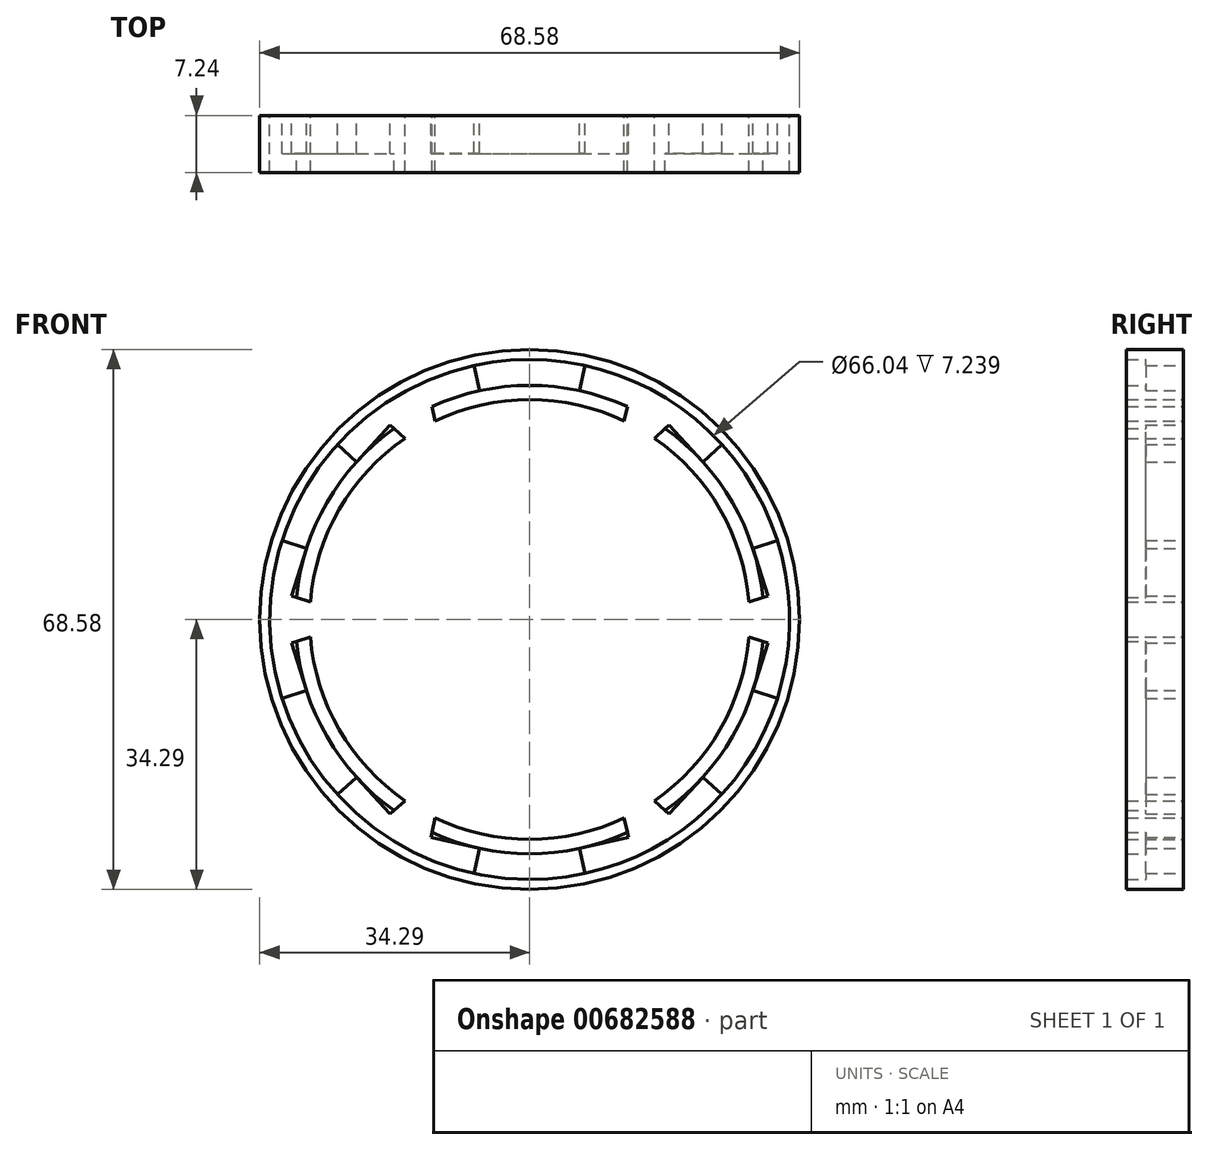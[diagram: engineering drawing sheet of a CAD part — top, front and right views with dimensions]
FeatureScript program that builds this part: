
annotation { "Feature Type Name" : "Feature", "Feature Type Description" : "" }
export const myFeature = defineFeature(function(context is Context, id is Id, definition is map)
    precondition{}
    {
        {
            var Q0;
            Q0=qCreatedBy(makeId("Front.planeOp"),FACE);
            var sketch = newSketch(context, id + "F0", { "sketchPlane" : qUnion([Q0])});
            skCircle(sketch, "E0", {"center": v(0, 0) * mm, "radius": 34.3 * mm});
            skArc(sketch, "E1", {"start": v(-15.84, 23.02) * mm, "mid": v(-24.2, 13.97) * mm, "end": v(-27.85, 2.21) * mm});
            skLineSegment(sketch, "E2", {"start": v(-7.05, 32.26) * mm, "end": v(-6.35, 29.06) * mm});
            skLineSegment(sketch, "E3", {"start": v(-6.35, 29.06) * mm, "end": v(-12.55, 27.7) * mm});
            skLineSegment(sketch, "E4", {"start": v(-12.55, 27.7) * mm, "end": v(-12.01, 25.23) * mm});
            skLineSegment(sketch, "E5", {"start": v(-18.86, 30.98) * mm, "end": v(0, 35.1) * mm, "construction": true});
            skLineSegment(sketch, "E6.MirrorCS", {"start": v(7.05, 32.26) * mm, "end": v(6.35, 29.06) * mm});
            skLineSegment(sketch, "E7.MirrorCS", {"start": v(6.35, 29.06) * mm, "end": v(12.55, 27.7) * mm});
            skLineSegment(sketch, "E8.MirrorCS", {"start": v(12.55, 27.7) * mm, "end": v(12.01, 25.23) * mm});
            skLineSegment(sketch, "E9.1.0", {"start": v(-31.46, 10.03) * mm, "end": v(-28.34, 9.03) * mm});
            skLineSegment(sketch, "E9.1.1", {"start": v(-28.34, 9.03) * mm, "end": v(-30.27, 2.98) * mm});
            skLineSegment(sketch, "E9.1.2", {"start": v(-30.27, 2.98) * mm, "end": v(-27.85, 2.21) * mm});
            skLineSegment(sketch, "E9.1.3", {"start": v(-17.72, 24.73) * mm, "end": v(-15.84, 23.02) * mm});
            skLineSegment(sketch, "E9.1.4", {"start": v(-22, 20.03) * mm, "end": v(-17.72, 24.73) * mm});
            skLineSegment(sketch, "E9.1.5", {"start": v(-24.41, 22.23) * mm, "end": v(-22, 20.03) * mm});
            skLineSegment(sketch, "E9.2.0", {"start": v(-24.41, -22.23) * mm, "end": v(-22, -20.03) * mm});
            skLineSegment(sketch, "E9.2.1", {"start": v(-22, -20.03) * mm, "end": v(-17.72, -24.73) * mm});
            skLineSegment(sketch, "E9.2.2", {"start": v(-17.72, -24.73) * mm, "end": v(-15.84, -23.02) * mm});
            skLineSegment(sketch, "E9.2.3", {"start": v(-30.27, -2.98) * mm, "end": v(-27.85, -2.21) * mm});
            skLineSegment(sketch, "E9.2.4", {"start": v(-28.34, -9.03) * mm, "end": v(-30.27, -2.98) * mm});
            skLineSegment(sketch, "E9.2.5", {"start": v(-31.46, -10.03) * mm, "end": v(-28.34, -9.03) * mm});
            skLineSegment(sketch, "E9.3.0", {"start": v(7.05, -32.26) * mm, "end": v(6.35, -29.06) * mm});
            skLineSegment(sketch, "E9.3.1", {"start": v(6.35, -29.06) * mm, "end": v(12.55, -27.7) * mm});
            skLineSegment(sketch, "E9.3.2", {"start": v(12.55, -27.7) * mm, "end": v(12.01, -25.23) * mm});
            skLineSegment(sketch, "E9.3.3", {"start": v(-12.55, -27.7) * mm, "end": v(-12.01, -25.23) * mm});
            skLineSegment(sketch, "E9.3.4", {"start": v(-6.35, -29.06) * mm, "end": v(-12.55, -27.7) * mm});
            skLineSegment(sketch, "E9.3.5", {"start": v(-7.05, -32.26) * mm, "end": v(-6.35, -29.06) * mm});
            skLineSegment(sketch, "E9.4.0", {"start": v(31.46, -10.03) * mm, "end": v(28.34, -9.03) * mm});
            skLineSegment(sketch, "E9.4.1", {"start": v(28.34, -9.03) * mm, "end": v(30.27, -2.98) * mm});
            skLineSegment(sketch, "E9.4.2", {"start": v(30.27, -2.98) * mm, "end": v(27.85, -2.21) * mm});
            skLineSegment(sketch, "E9.4.3", {"start": v(17.72, -24.73) * mm, "end": v(15.84, -23.02) * mm});
            skLineSegment(sketch, "E9.4.4", {"start": v(22, -20.03) * mm, "end": v(17.72, -24.73) * mm});
            skLineSegment(sketch, "E9.4.5", {"start": v(24.41, -22.23) * mm, "end": v(22, -20.03) * mm});
            skLineSegment(sketch, "E9.5.0", {"start": v(24.41, 22.23) * mm, "end": v(22, 20.03) * mm});
            skLineSegment(sketch, "E9.5.1", {"start": v(22, 20.03) * mm, "end": v(17.72, 24.73) * mm});
            skLineSegment(sketch, "E9.5.2", {"start": v(17.72, 24.73) * mm, "end": v(15.84, 23.02) * mm});
            skLineSegment(sketch, "E9.5.3", {"start": v(30.27, 2.98) * mm, "end": v(27.85, 2.21) * mm});
            skLineSegment(sketch, "E9.5.4", {"start": v(28.34, 9.03) * mm, "end": v(30.27, 2.98) * mm});
            skLineSegment(sketch, "E9.5.5", {"start": v(31.46, 10.03) * mm, "end": v(28.34, 9.03) * mm});
            skArc(sketch, "E10.trimOffspring", {"start": v(-27.85, -2.21) * mm, "mid": v(-24.2, -13.97) * mm, "end": v(-15.84, -23.02) * mm});
            skArc(sketch, "E11.trimOffspring", {"start": v(-12.01, -25.23) * mm, "mid": v(0, -27.94) * mm, "end": v(12.01, -25.23) * mm});
            skArc(sketch, "E12.trimOffspring", {"start": v(15.84, -23.02) * mm, "mid": v(24.2, -13.97) * mm, "end": v(27.85, -2.21) * mm});
            skArc(sketch, "E13.trimOffspring", {"start": v(27.85, 2.21) * mm, "mid": v(24.2, 13.97) * mm, "end": v(15.84, 23.02) * mm});
            skArc(sketch, "E14.trimOffspring", {"start": v(12.01, 25.23) * mm, "mid": v(0, 27.94) * mm, "end": v(-12.01, 25.23) * mm});
            skArc(sketch, "E15", {"start": v(-7.05, 32.26) * mm, "mid": v(-16.51, 28.6) * mm, "end": v(-24.41, 22.23) * mm});
            skPoint(sketch, "E16.orphan", {"position": v(7.32, 33.5) * mm});
            skPoint(sketch, "E17.orphan", {"position": v(-7.32, 33.5) * mm});
            skPoint(sketch, "E18.orphan", {"position": v(-25.35, 23.09) * mm});
            skArc(sketch, "E19.trimOffspring", {"start": v(-31.46, 10.03) * mm, "mid": v(-33.02, 0) * mm, "end": v(-31.46, -10.03) * mm});
            skPoint(sketch, "E20.orphan", {"position": v(-32.67, 10.41) * mm});
            skPoint(sketch, "E21.orphan", {"position": v(-32.67, -10.41) * mm});
            skArc(sketch, "E22.trimOffspring", {"start": v(-24.41, -22.23) * mm, "mid": v(-16.51, -28.6) * mm, "end": v(-7.05, -32.26) * mm});
            skPoint(sketch, "E23.orphan", {"position": v(-25.35, -23.09) * mm});
            skPoint(sketch, "E24.orphan", {"position": v(-7.32, -33.5) * mm});
            skArc(sketch, "E25.trimOffspring", {"start": v(7.05, -32.26) * mm, "mid": v(16.5, -28.6) * mm, "end": v(24.41, -22.23) * mm});
            skPoint(sketch, "E26.orphan", {"position": v(7.32, -33.5) * mm});
            skPoint(sketch, "E27.orphan", {"position": v(25.35, -23.09) * mm});
            skArc(sketch, "E28.trimOffspring", {"start": v(31.46, -10.03) * mm, "mid": v(33.02, 0) * mm, "end": v(31.46, 10.03) * mm});
            skPoint(sketch, "E29.orphan", {"position": v(32.67, -10.41) * mm});
            skPoint(sketch, "E30.orphan", {"position": v(32.67, 10.41) * mm});
            skArc(sketch, "E31.trimOffspring", {"start": v(24.41, 22.23) * mm, "mid": v(16.5, 28.6) * mm, "end": v(7.05, 32.26) * mm});
            skPoint(sketch, "E32.orphan", {"position": v(25.35, 23.09) * mm});
            skSolve(sketch);
        }
        {
            var Q0;
            Q0 = qSketchRegion(id + "F0", true);
            extrude(context, id + "F1", {"entities" : qUnion([Q0]), "endBound" : BoundingType.SYMMETRIC, "depth" : 4.83 * mm, "offsetDistance" : 25.4 * mm});
        }
        {
            var Q0;
            Q0=makeQuery(id+"F1.opExtrude","CAP_FACE",FACE,{"disambiguationData":[OSD([sQuery(id+"F0.wireOp",EDGE,"E0"),sQuery(id+"F0.wireOp",EDGE,"E1"),sQuery(id+"F0.wireOp",EDGE,"E2"),sQuery(id+"F0.wireOp",EDGE,"E3"),sQuery(id+"F0.wireOp",EDGE,"E4"),sQuery(id+"F0.wireOp",EDGE,"E6.MirrorCS"),sQuery(id+"F0.wireOp",EDGE,"E7.MirrorCS"),sQuery(id+"F0.wireOp",EDGE,"E8.MirrorCS"),sQuery(id+"F0.wireOp",EDGE,"E9.1.0"),sQuery(id+"F0.wireOp",EDGE,"E9.1.1"),sQuery(id+"F0.wireOp",EDGE,"E9.1.2"),sQuery(id+"F0.wireOp",EDGE,"E9.1.3"),sQuery(id+"F0.wireOp",EDGE,"E9.1.4"),sQuery(id+"F0.wireOp",EDGE,"E9.1.5"),sQuery(id+"F0.wireOp",EDGE,"E9.2.0"),sQuery(id+"F0.wireOp",EDGE,"E9.2.1"),sQuery(id+"F0.wireOp",EDGE,"E9.2.2"),sQuery(id+"F0.wireOp",EDGE,"E9.2.3"),sQuery(id+"F0.wireOp",EDGE,"E9.2.4"),sQuery(id+"F0.wireOp",EDGE,"E9.2.5"),sQuery(id+"F0.wireOp",EDGE,"E9.3.0"),sQuery(id+"F0.wireOp",EDGE,"E9.3.1"),sQuery(id+"F0.wireOp",EDGE,"E9.3.2"),sQuery(id+"F0.wireOp",EDGE,"E9.3.3"),sQuery(id+"F0.wireOp",EDGE,"E9.3.4"),sQuery(id+"F0.wireOp",EDGE,"E9.3.5"),sQuery(id+"F0.wireOp",EDGE,"E9.4.0"),sQuery(id+"F0.wireOp",EDGE,"E9.4.1"),sQuery(id+"F0.wireOp",EDGE,"E9.4.2"),sQuery(id+"F0.wireOp",EDGE,"E9.4.3"),sQuery(id+"F0.wireOp",EDGE,"E9.4.4"),sQuery(id+"F0.wireOp",EDGE,"E9.4.5"),sQuery(id+"F0.wireOp",EDGE,"E9.5.0"),sQuery(id+"F0.wireOp",EDGE,"E9.5.1"),sQuery(id+"F0.wireOp",EDGE,"E9.5.2"),sQuery(id+"F0.wireOp",EDGE,"E9.5.3"),sQuery(id+"F0.wireOp",EDGE,"E9.5.4"),sQuery(id+"F0.wireOp",EDGE,"E9.5.5"),sQuery(id+"F0.wireOp",EDGE,"E10.trimOffspring"),sQuery(id+"F0.wireOp",EDGE,"E11.trimOffspring"),sQuery(id+"F0.wireOp",EDGE,"E12.trimOffspring"),sQuery(id+"F0.wireOp",EDGE,"E13.trimOffspring"),sQuery(id+"F0.wireOp",EDGE,"E14.trimOffspring"),sQuery(id+"F0.wireOp",EDGE,"E15"),sQuery(id+"F0.wireOp",EDGE,"E19.trimOffspring"),sQuery(id+"F0.wireOp",EDGE,"E22.trimOffspring"),sQuery(id+"F0.wireOp",EDGE,"E25.trimOffspring"),sQuery(id+"F0.wireOp",EDGE,"E28.trimOffspring"),sQuery(id+"F0.wireOp",EDGE,"E31.trimOffspring")])],"isStart":false});
            var sketch = newSketch(context, id + "F2", { "sketchPlane" : qUnion([Q0])});
            skCircle(sketch, "E33", {"center": v(0, 0) * mm, "radius": 33.02 * mm});
            skArc(sketch, "E34", {"start": v(-17.21, 24.26) * mm, "mid": v(-25.76, 14.87) * mm, "end": v(-29.62, 2.77) * mm});
            skArc(sketch, "E35", {"start": v(-15.84, 23.02) * mm, "mid": v(-24.2, 13.97) * mm, "end": v(-27.85, 2.21) * mm});
            skCircle(sketch, "E36", {"center": v(0, 0) * mm, "radius": 34.3 * mm});
            skLineSegment(sketch, "E37.0", {"start": v(-17.21, 24.26) * mm, "end": v(-15.84, 23.02) * mm});
            skLineSegment(sketch, "E37.1", {"start": v(-12.4, 27.04) * mm, "end": v(-12.01, 25.23) * mm});
            skLineSegment(sketch, "E37.2", {"start": v(12.4, 27.04) * mm, "end": v(12.01, 25.23) * mm});
            skLineSegment(sketch, "E37.3", {"start": v(17.21, 24.26) * mm, "end": v(15.84, 23.02) * mm});
            skLineSegment(sketch, "E37.4", {"start": v(29.62, 2.77) * mm, "end": v(27.85, 2.21) * mm});
            skLineSegment(sketch, "E37.5", {"start": v(29.62, -2.77) * mm, "end": v(27.85, -2.21) * mm});
            skLineSegment(sketch, "E37.6", {"start": v(17.21, -24.26) * mm, "end": v(15.84, -23.02) * mm});
            skLineSegment(sketch, "E37.7", {"start": v(12.4, -27.04) * mm, "end": v(12.01, -25.23) * mm});
            skLineSegment(sketch, "E37.8", {"start": v(-12.4, -27.04) * mm, "end": v(-12.01, -25.23) * mm});
            skLineSegment(sketch, "E37.9", {"start": v(-17.21, -24.26) * mm, "end": v(-15.84, -23.02) * mm});
            skLineSegment(sketch, "E37.10", {"start": v(-29.62, 2.77) * mm, "end": v(-27.85, 2.21) * mm});
            skLineSegment(sketch, "E37.11", {"start": v(-29.62, -2.77) * mm, "end": v(-27.85, -2.21) * mm});
            skPoint(sketch, "E38.orphan", {"position": v(-17.72, 24.73) * mm});
            skPoint(sketch, "E39.orphan", {"position": v(-12.55, 27.7) * mm});
            skPoint(sketch, "E40.orphan", {"position": v(12.55, 27.7) * mm});
            skArc(sketch, "E41.trimOffspring", {"start": v(12.4, 27.04) * mm, "mid": v(0, 29.75) * mm, "end": v(-12.4, 27.04) * mm});
            skArc(sketch, "E42.trimOffspring", {"start": v(12.01, 25.23) * mm, "mid": v(0, 27.94) * mm, "end": v(-12.01, 25.23) * mm});
            skPoint(sketch, "E43.orphan", {"position": v(17.72, 24.73) * mm});
            skPoint(sketch, "E44.orphan", {"position": v(30.27, 2.98) * mm});
            skArc(sketch, "E45.trimOffspring", {"start": v(29.62, 2.77) * mm, "mid": v(25.76, 14.87) * mm, "end": v(17.21, 24.26) * mm});
            skArc(sketch, "E46.trimOffspring", {"start": v(27.85, 2.21) * mm, "mid": v(24.2, 13.97) * mm, "end": v(15.84, 23.02) * mm});
            skPoint(sketch, "E47.orphan", {"position": v(30.27, -2.98) * mm});
            skPoint(sketch, "E48.orphan", {"position": v(17.72, -24.73) * mm});
            skPoint(sketch, "E49.orphan", {"position": v(12.55, -27.7) * mm});
            skArc(sketch, "E50.trimOffspring", {"start": v(15.84, -23.02) * mm, "mid": v(24.2, -13.97) * mm, "end": v(27.85, -2.21) * mm});
            skArc(sketch, "E51.trimOffspring", {"start": v(17.21, -24.26) * mm, "mid": v(25.76, -14.87) * mm, "end": v(29.62, -2.77) * mm});
            skArc(sketch, "E52.trimOffspring", {"start": v(-12.4, -27.04) * mm, "mid": v(0, -29.75) * mm, "end": v(12.4, -27.04) * mm});
            skArc(sketch, "E53.trimOffspring", {"start": v(-12.01, -25.23) * mm, "mid": v(0, -27.94) * mm, "end": v(12.01, -25.23) * mm});
            skPoint(sketch, "E54.orphan", {"position": v(-12.55, -27.7) * mm});
            skPoint(sketch, "E55.orphan", {"position": v(-17.72, -24.73) * mm});
            skArc(sketch, "E56.trimOffspring", {"start": v(-27.85, -2.21) * mm, "mid": v(-24.2, -13.97) * mm, "end": v(-15.84, -23.02) * mm});
            skArc(sketch, "E57.trimOffspring", {"start": v(-29.62, -2.77) * mm, "mid": v(-25.76, -14.87) * mm, "end": v(-17.21, -24.26) * mm});
            skPoint(sketch, "E58.orphan", {"position": v(-30.27, 2.98) * mm});
            skPoint(sketch, "E59.orphan", {"position": v(-30.27, -2.98) * mm});
            skSolve(sketch);
        }
        {
            var Q0;
            Q0 = qSketchRegion(id + "F2", true);
            var Q1;
            Q1=makeQuery(id+"F2.imprint","IMPRINT",FACE,{"disambiguationData":[TD([[makeQuery(id+"F2.imprint","IMPRINT",EDGE,{"derivedFrom":sQuery(id+"F2.wireOp",EDGE,"E35")}),-1.0]])]});
            var Q2;
            {var subQ4=sQuery(id+"F2.wireOp",EDGE,"E37.1");Q2=makeQuery(id+"F2.imprint","IMPRINT",FACE,{"disambiguationData":[TD([[makeQuery(id+"F2.imprint","IMPRINT",EDGE,{"derivedFrom":subQ4}),1.0]])]});}
            var Q3;
            {var subQ4=sQuery(id+"F2.wireOp",EDGE,"E37.3");Q3=makeQuery(id+"F2.imprint","IMPRINT",FACE,{"disambiguationData":[TD([[makeQuery(id+"F2.imprint","IMPRINT",EDGE,{"derivedFrom":subQ4}),1.0]])]});}
            var Q4;
            {var subQ4=sQuery(id+"F2.wireOp",EDGE,"E37.7");Q4=makeQuery(id+"F2.imprint","IMPRINT",FACE,{"disambiguationData":[TD([[makeQuery(id+"F2.imprint","IMPRINT",EDGE,{"derivedFrom":subQ4}),1.0]])]});}
            var Q5;
            {var subQ3=sQuery(id+"F2.wireOp",EDGE,"E37.9");Q5=makeQuery(id+"F2.imprint","IMPRINT",FACE,{"disambiguationData":[TD([[makeQuery(id+"F2.imprint","IMPRINT",EDGE,{"derivedFrom":subQ3}),1.0]])]});}
            var Q6;
            {var subQ3=sQuery(id+"F2.wireOp",EDGE,"E37.5");Q6=makeQuery(id+"F2.imprint","IMPRINT",FACE,{"disambiguationData":[TD([[makeQuery(id+"F2.imprint","IMPRINT",EDGE,{"derivedFrom":subQ3}),1.0]])]});}
            extrude(context, id + "F3", {"entities" : qUnion([Q0, Q1, Q2, Q3, Q4, Q5, Q6]), "operationType" : NewBodyOperationType.ADD, "depth" : 2.41 * mm, "offsetDistance" : 25.4 * mm});
        }
        {
            var Q0;
            Q0=makeQuery(id+"F3.opExtrude","CAP_FACE",FACE,{"disambiguationData":[OSD([sQuery(id+"F2.wireOp",EDGE,"E33"),sQuery(id+"F2.wireOp",EDGE,"E36")])],"isStart":false});
            var sketch = newSketch(context, id + "F4", { "sketchPlane" : qUnion([Q0])});
            skArc(sketch, "E60.0", {"start": v(-6.35, 29.06) * mm, "mid": v(-9.43, 28.21) * mm, "end": v(-12.4, 27.04) * mm});
            skLineSegment(sketch, "E60.1", {"start": v(-7.05, 32.26) * mm, "end": v(-6.35, 29.06) * mm});
            skArc(sketch, "E60.2", {"start": v(-7.05, 32.26) * mm, "mid": v(-10.81, 31.2) * mm, "end": v(-14.42, 29.7) * mm});
            skLineSegment(sketch, "E61", {"start": v(-12.4, 27.04) * mm, "end": v(-14.42, 29.7) * mm});
            skPoint(sketch, "E62.orphan", {"position": v(12.4, 27.04) * mm});
            skLineSegment(sketch, "E63.MirrorCS", {"start": v(7.05, 32.26) * mm, "end": v(6.35, 29.06) * mm});
            skLineSegment(sketch, "E64.MirrorCS", {"start": v(12.4, 27.04) * mm, "end": v(14.42, 29.7) * mm});
            skArc(sketch, "E65.MirrorCS", {"start": v(6.35, 29.06) * mm, "mid": v(9.43, 28.21) * mm, "end": v(12.4, 27.04) * mm});
            skArc(sketch, "E66.MirrorCS", {"start": v(7.05, 32.26) * mm, "mid": v(10.81, 31.2) * mm, "end": v(14.42, 29.7) * mm});
            skSolve(sketch);
        }
        {
            var Q0;
            Q0 = qSketchRegion(id + "F4", true);
            extrude(context, id + "F5", {"entities" : qUnion([Q0]), "operationType" : NewBodyOperationType.REMOVE, "oppositeDirection" : true, "depth" : 43.69 * mm, "offsetDistance" : 25.4 * mm});
        }
    });
